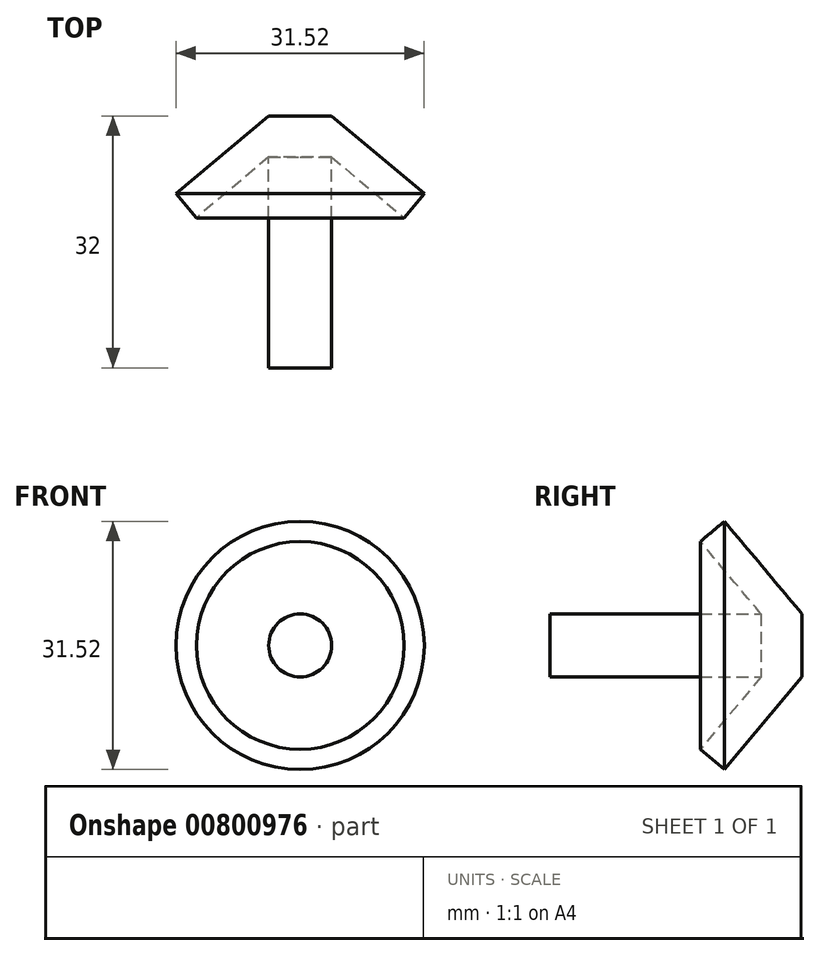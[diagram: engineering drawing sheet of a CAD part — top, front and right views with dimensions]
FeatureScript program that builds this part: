
annotation { "Feature Type Name" : "Feature", "Feature Type Description" : "" }
export const myFeature = defineFeature(function(context is Context, id is Id, definition is map)
    precondition{}
    {
        {
            var Q0;
            Q0=qCreatedBy(makeId("Top.planeOp"),FACE);
            var sketch = newSketch(context, id + "F0", { "sketchPlane" : qUnion([Q0])});
            skLineSegment(sketch, "E0", {"start": v(0, 0) * mm, "end": v(0, -32) * mm});
            skLineSegment(sketch, "E1", {"start": v(0, -32) * mm, "end": v(4, -32) * mm});
            skLineSegment(sketch, "E2", {"start": v(4, -32) * mm, "end": v(4, -5.22) * mm});
            skLineSegment(sketch, "E3", {"start": v(4, -5.22) * mm, "end": v(13.2, -12.94) * mm});
            skLineSegment(sketch, "E4", {"start": v(13.2, -12.94) * mm, "end": v(15.76, -9.87) * mm});
            skLineSegment(sketch, "E5", {"start": v(15.76, -9.87) * mm, "end": v(4, 0) * mm});
            skLineSegment(sketch, "E6", {"start": v(4, 0) * mm, "end": v(0, 0) * mm});
            skSolve(sketch);
        }
        {
            var Q0;
            Q0=makeQuery(id+"F0.imprint","IMPRINT",FACE,{"disambiguationData":[TD([[makeQuery(id+"F0.imprint","IMPRINT",EDGE,{"derivedFrom":sQuery(id+"F0.wireOp",EDGE,"E0")}),1.0]])]});
            var Q1;
            Q1=sQuery(id+"F0.wireOp",EDGE,"E0");
            revolve(context, id + "F1", {"surfaceOperationType" : NewSurfaceOperationType.NEW, "entities" : qUnion([Q0]), "axis" : qUnion([Q1]), "revolveType" : RevolveType.FULL});
        }
    });
